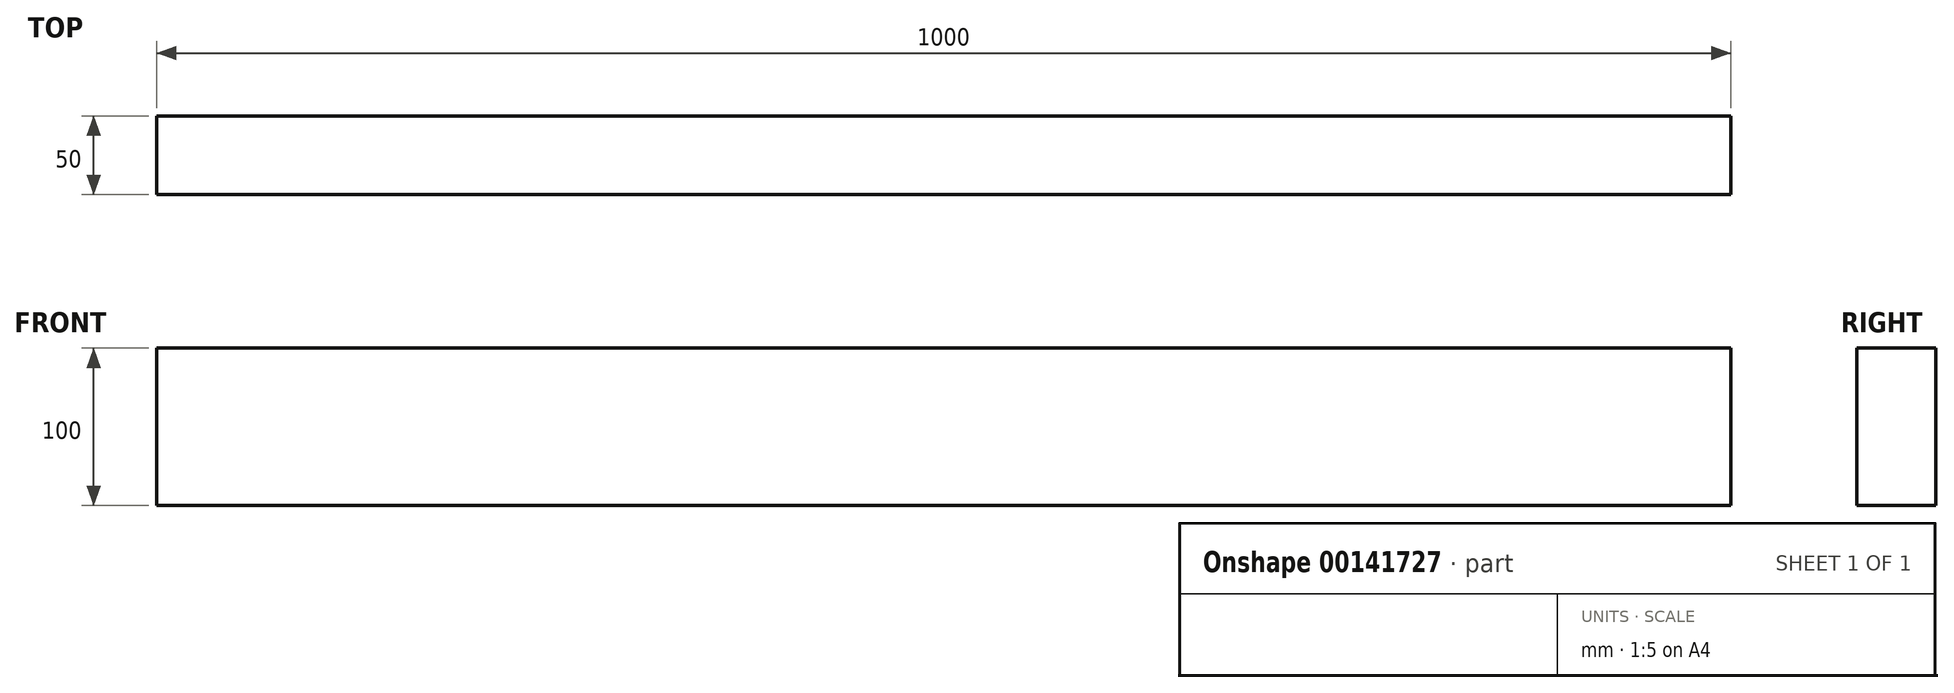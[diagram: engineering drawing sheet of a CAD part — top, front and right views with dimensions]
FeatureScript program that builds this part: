
annotation { "Feature Type Name" : "Feature", "Feature Type Description" : "" }
export const myFeature = defineFeature(function(context is Context, id is Id, definition is map)
    precondition{}
    {
        {
            var Q0;
            Q0=qCreatedBy(makeId("Top.planeOp"),FACE);
            var sketch = newSketch(context, id + "F0", { "sketchPlane" : qUnion([Q0])});
            skLineSegment(sketch, "E0.bottom", {"start": v(500, 25) * mm, "end": v(-500, 25) * mm});
            skLineSegment(sketch, "E0.top", {"start": v(500, -25) * mm, "end": v(-500, -25) * mm});
            skLineSegment(sketch, "E0.left", {"start": v(500, 25) * mm, "end": v(500, -25) * mm});
            skLineSegment(sketch, "E0.right", {"start": v(-500, 25) * mm, "end": v(-500, -25) * mm});
            skPoint(sketch, "E0.middle", {"position": v(0, 0) * mm});
            skSolve(sketch);
        }
        {
            var Q0;
            Q0=makeQuery(id+"F0.imprint","IMPRINT",FACE,{"disambiguationData":[TD([[makeQuery(id+"F0.imprint","IMPRINT",EDGE,{"derivedFrom":sQuery(id+"F0.wireOp",EDGE,"E0.bottom")}),1.0]])]});
            extrude(context, id + "F1", {"entities" : qUnion([Q0]), "depth" : 100 * mm});
        }
    });
